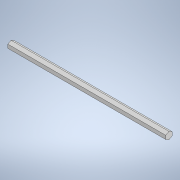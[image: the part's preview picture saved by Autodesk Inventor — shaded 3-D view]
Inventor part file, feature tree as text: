
AUTODESK INVENTOR PART (.ipt)
format: ipt  version: 2020.2 (Build 242310000, 310)  size: 94,208 bytes
history: native  units: in
note: dims shown in document units (in); Inventor stores cm internally (conversion verified against a paired STEP export)
features: extrude x1, sketch x1
ambient origin geometry x8: Origin, YZ Plane, XZ Plane, XY Plane, X Axis, Y Axis, Z Axis, Center Point
bodies: Solid1 (feature_tree)
feature tree (2):
  extrude  "Extrusion1"  [1 undecoded]
  sketch  "Sketch1"  dims[d0=5.3125in d1=0.0in]
note: 1 required parameter value undecoded (feature->parameter linkage not recoverable at this tier; creation-order binding heuristic only, values carry confidence <= 0.55)
